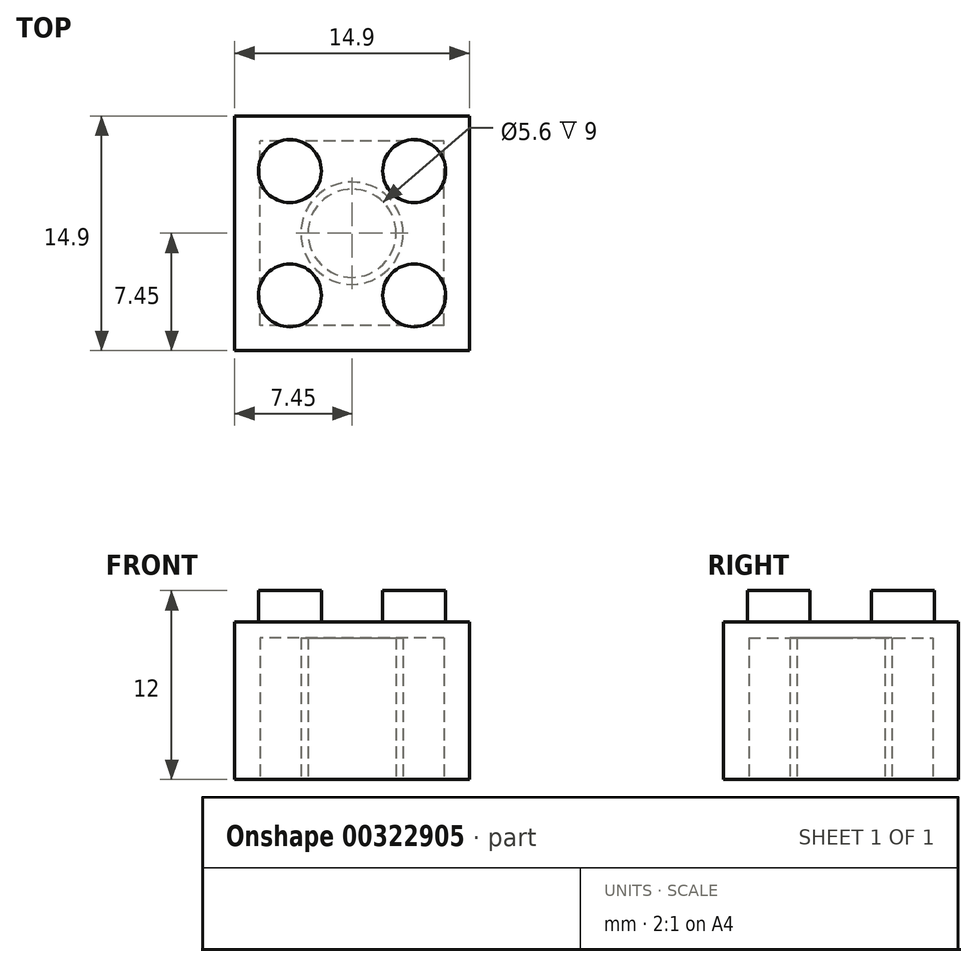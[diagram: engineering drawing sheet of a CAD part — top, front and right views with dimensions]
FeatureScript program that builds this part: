
annotation { "Feature Type Name" : "Feature", "Feature Type Description" : "" }
export const myFeature = defineFeature(function(context is Context, id is Id, definition is map)
    precondition{}
    {
        {
            var Q0;
            Q0=qCreatedBy(makeId("Top.planeOp"),FACE);
            var sketch = newSketch(context, id + "F0", { "sketchPlane" : qUnion([Q0])});
            skLineSegment(sketch, "E0.bottom", {"start": v(7.45, 7.45) * mm, "end": v(-7.45, 7.45) * mm});
            skLineSegment(sketch, "E0.top", {"start": v(7.45, -7.45) * mm, "end": v(-7.45, -7.45) * mm});
            skLineSegment(sketch, "E0.left", {"start": v(7.45, 7.45) * mm, "end": v(7.45, -7.45) * mm});
            skLineSegment(sketch, "E0.right", {"start": v(-7.45, 7.45) * mm, "end": v(-7.45, -7.45) * mm});
            skPoint(sketch, "E0.middle", {"position": v(0, 0) * mm});
            skCircle(sketch, "E1", {"center": v(-3.95, 3.95) * mm, "radius": 2 * mm});
            skCircle(sketch, "E2", {"center": v(3.95, 3.95) * mm, "radius": 2 * mm});
            skCircle(sketch, "E3", {"center": v(3.95, -3.95) * mm, "radius": 2 * mm});
            skCircle(sketch, "E4", {"center": v(-3.95, -3.95) * mm, "radius": 2 * mm});
            skSolve(sketch);
        }
        {
            var Q0;
            Q0=makeQuery(id+"F0.imprint","IMPRINT",FACE,{"disambiguationData":[TD([[makeQuery(id+"F0.imprint","IMPRINT",EDGE,{"derivedFrom":sQuery(id+"F0.wireOp",EDGE,"E0.bottom")}),1.0]])]});
            extrude(context, id + "F1", {"entities" : qUnion([Q0]), "depth" : 10 * mm});
        }
        {
            var Q0;
            Q0=makeQuery(id+"F0.imprint","IMPRINT",FACE,{"disambiguationData":[TD([[makeQuery(id+"F0.imprint","IMPRINT",EDGE,{"derivedFrom":sQuery(id+"F0.wireOp",EDGE,"E4")}),1.0]])]});
            var Q1;
            Q1=makeQuery(id+"F0.imprint","IMPRINT",FACE,{"disambiguationData":[TD([[makeQuery(id+"F0.imprint","IMPRINT",EDGE,{"derivedFrom":sQuery(id+"F0.wireOp",EDGE,"E1")}),1.0]])]});
            var Q2;
            Q2=makeQuery(id+"F0.imprint","IMPRINT",FACE,{"disambiguationData":[TD([[makeQuery(id+"F0.imprint","IMPRINT",EDGE,{"derivedFrom":sQuery(id+"F0.wireOp",EDGE,"E2")}),1.0]])]});
            var Q3;
            Q3=makeQuery(id+"F0.imprint","IMPRINT",FACE,{"disambiguationData":[TD([[makeQuery(id+"F0.imprint","IMPRINT",EDGE,{"derivedFrom":sQuery(id+"F0.wireOp",EDGE,"E3")}),1.0]])]});
            extrude(context, id + "F2", {"entities" : qUnion([Q0, Q1, Q2, Q3]), "operationType" : NewBodyOperationType.ADD, "depth" : 12 * mm});
        }
        {
            var Q0;
            {var subQ0=sQuery(id+"F0.wireOp",EDGE,"E4");var subQ1=sQuery(id+"F0.wireOp",EDGE,"E3");var subQ2=sQuery(id+"F0.wireOp",EDGE,"E2");var subQ3=sQuery(id+"F0.wireOp",EDGE,"E1");Q0=makeQuery(id+"F2.boolean.opBoolean","MERGE",FACE,{"derivedFrom":[makeQuery(id+"F1.opExtrude","CAP_FACE",FACE,{"disambiguationData":[OSD([sQuery(id+"F0.wireOp",EDGE,"E0.bottom"),sQuery(id+"F0.wireOp",EDGE,"E0.top"),sQuery(id+"F0.wireOp",EDGE,"E0.left"),sQuery(id+"F0.wireOp",EDGE,"E0.right"),subQ3,subQ2,subQ1,subQ0])],"isStart":true}),makeQuery(id+"F2.opExtrude","CAP_FACE",FACE,{"disambiguationData":[OSD([subQ3])],"isStart":true}),makeQuery(id+"F2.opExtrude","CAP_FACE",FACE,{"disambiguationData":[OSD([subQ2])],"isStart":true}),makeQuery(id+"F2.opExtrude","CAP_FACE",FACE,{"disambiguationData":[OSD([subQ1])],"isStart":true}),makeQuery(id+"F2.opExtrude","CAP_FACE",FACE,{"disambiguationData":[OSD([subQ0])],"isStart":true})]});}
            var sketch = newSketch(context, id + "F3", { "sketchPlane" : qUnion([Q0])});
            skCircle(sketch, "E5", {"center": v(0, 0) * mm, "radius": 3.25 * mm});
            skCircle(sketch, "E6", {"center": v(0, 0) * mm, "radius": 2.8 * mm});
            skLineSegment(sketch, "E7.bottom", {"start": v(5.85, 5.85) * mm, "end": v(-5.85, 5.85) * mm});
            skLineSegment(sketch, "E7.top", {"start": v(5.85, -5.85) * mm, "end": v(-5.85, -5.85) * mm});
            skLineSegment(sketch, "E7.left", {"start": v(5.85, 5.85) * mm, "end": v(5.85, -5.85) * mm});
            skLineSegment(sketch, "E7.right", {"start": v(-5.85, 5.85) * mm, "end": v(-5.85, -5.85) * mm});
            skSolve(sketch);
        }
        {
            var Q0;
            Q0=makeQuery(id+"F3.imprint","IMPRINT",FACE,{"disambiguationData":[TD([[makeQuery(id+"F3.imprint","IMPRINT",EDGE,{"derivedFrom":sQuery(id+"F3.wireOp",EDGE,"E5")}),-1.0]])]});
            var Q1;
            Q1=makeQuery(id+"F3.imprint","IMPRINT",FACE,{"disambiguationData":[TD([[makeQuery(id+"F3.imprint","IMPRINT",EDGE,{"derivedFrom":sQuery(id+"F3.wireOp",EDGE,"E6")}),1.0]])]});
            extrude(context, id + "F4", {"entities" : qUnion([Q0, Q1]), "operationType" : NewBodyOperationType.REMOVE, "oppositeDirection" : true, "depth" : 9 * mm});
        }
    });
